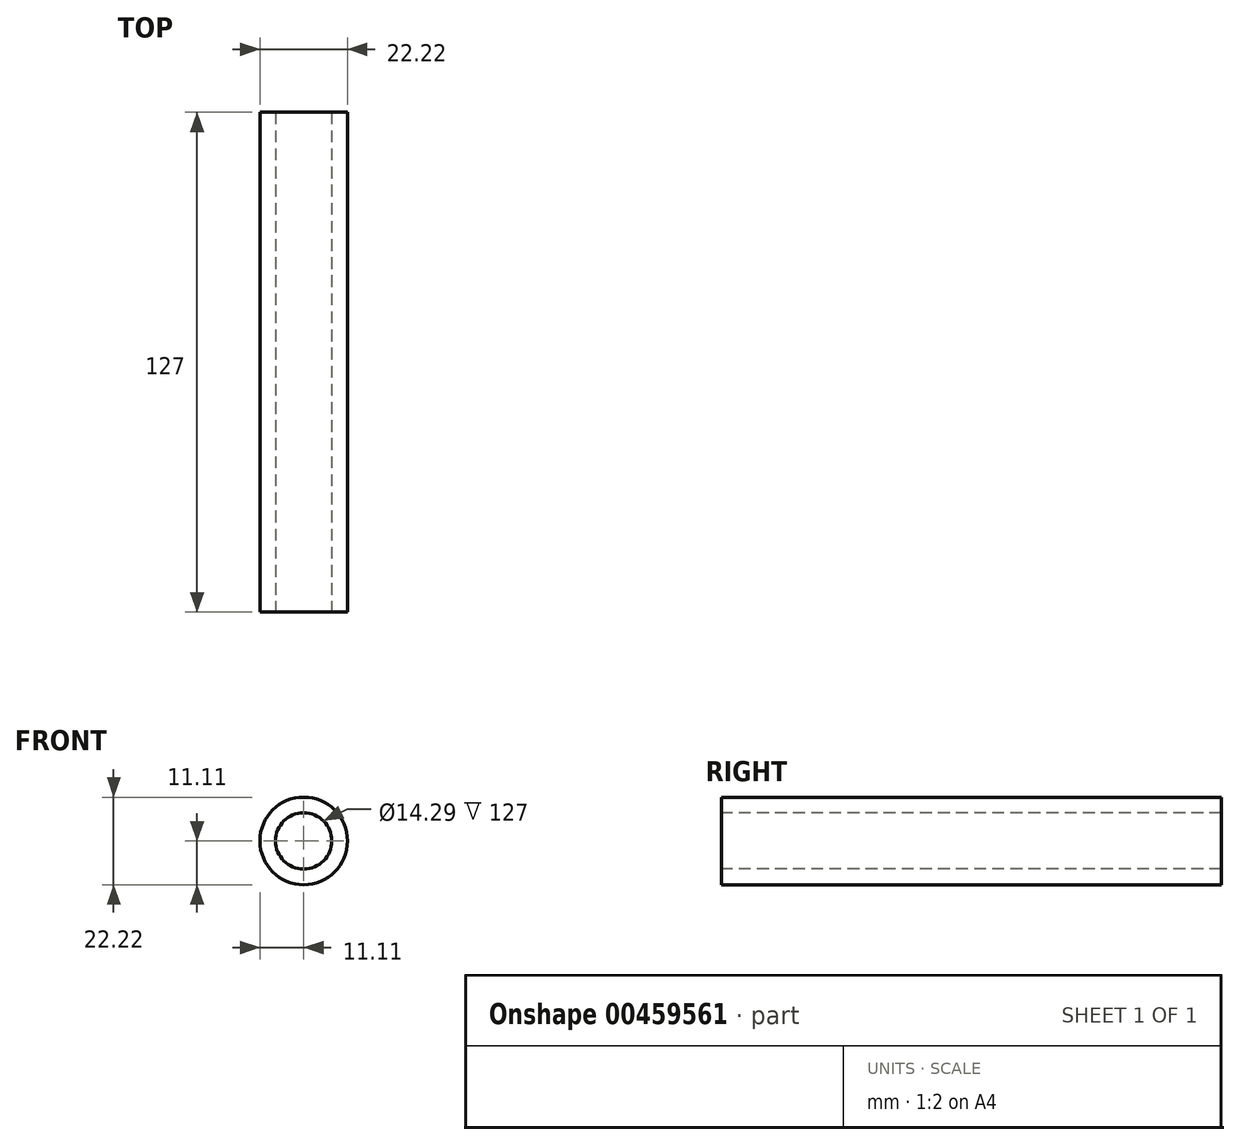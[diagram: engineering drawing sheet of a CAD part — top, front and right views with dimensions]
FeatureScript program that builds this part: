
annotation { "Feature Type Name" : "Feature", "Feature Type Description" : "" }
export const myFeature = defineFeature(function(context is Context, id is Id, definition is map)
    precondition{}
    {
        {
            var Q0;
            Q0=qCreatedBy(makeId("Front.planeOp"),FACE);
            var sketch = newSketch(context, id + "F0", { "sketchPlane" : qUnion([Q0])});
            skCircle(sketch, "E0", {"center": v(0, 0) * mm, "radius": 11.11 * mm});
            skSolve(sketch);
        }
        {
            var Q0;
            Q0=makeQuery(id+"F0.imprint","IMPRINT",FACE,{"disambiguationData":[TD([[makeQuery(id+"F0.imprint","IMPRINT",EDGE,{"derivedFrom":sQuery(id+"F0.wireOp",EDGE,"E0")}),1.0]])]});
            extrude(context, id + "F1", {"entities" : qUnion([Q0]), "endBound" : BoundingType.SYMMETRIC, "depth" : 127 * mm});
        }
        {
            var Q0;
            Q0=makeQuery(id+"F1.opExtrude","CAP_FACE",FACE,{"disambiguationData":[OSD([sQuery(id+"F0.wireOp",EDGE,"E0")])],"isStart":false});
            var sketch = newSketch(context, id + "F2", { "sketchPlane" : qUnion([Q0])});
            skCircle(sketch, "E1", {"center": v(0, 0) * mm, "radius": 7.14 * mm});
            skSolve(sketch);
        }
        {
            var Q0;
            Q0=qSketchRegion(id+"F2",true);
            extrude(context, id + "F3", {"entities" : qUnion([Q0]), "operationType" : NewBodyOperationType.REMOVE, "oppositeDirection" : true, "depth" : 127 * mm});
        }
    });
